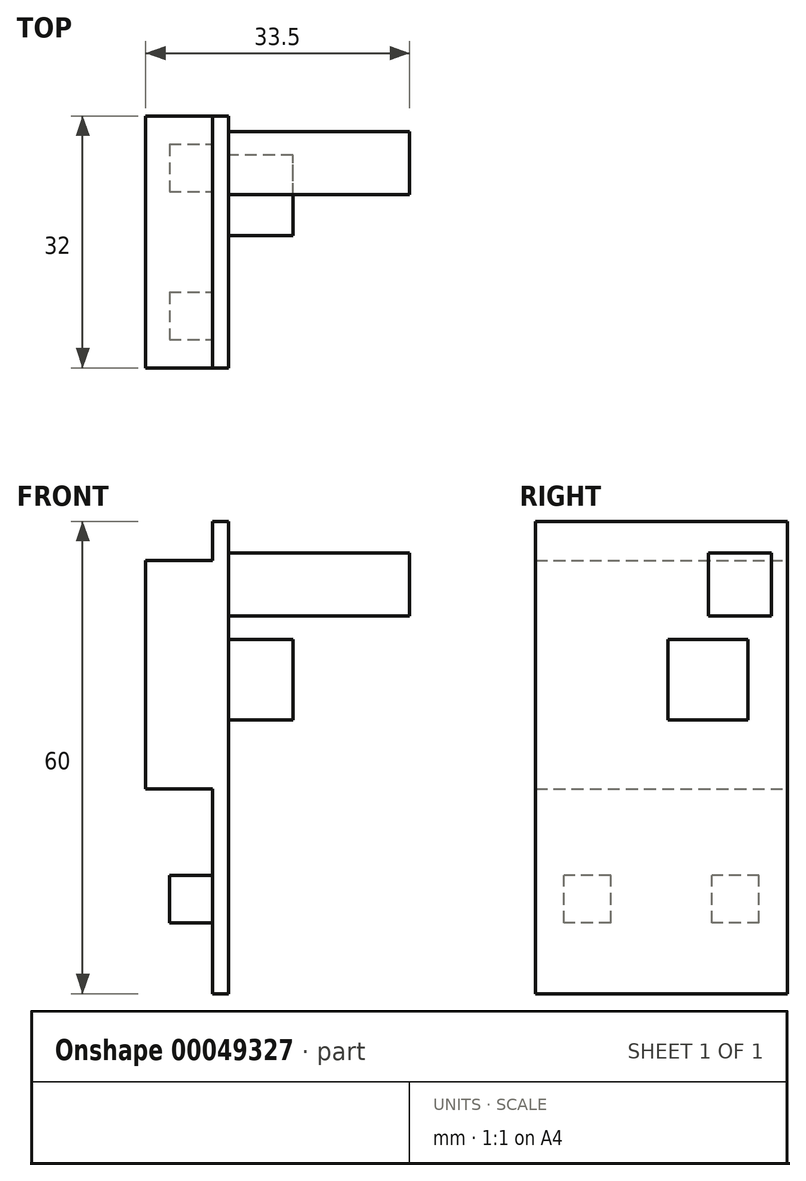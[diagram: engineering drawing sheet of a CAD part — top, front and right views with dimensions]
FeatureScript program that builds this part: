
annotation { "Feature Type Name" : "Feature", "Feature Type Description" : "" }
export const myFeature = defineFeature(function(context is Context, id is Id, definition is map)
    precondition{}
    {
        {
            var Q0;
            Q0=qCreatedBy(makeId("Right.planeOp"),FACE);
            var sketch = newSketch(context, id + "F0", { "sketchPlane" : qUnion([Q0])});
            skLineSegment(sketch, "E0.bottom", {"start": v(0, 0) * mm, "end": v(32, 0) * mm});
            skLineSegment(sketch, "E0.top", {"start": v(0, 60) * mm, "end": v(32, 60) * mm});
            skLineSegment(sketch, "E0.left", {"start": v(0, 0) * mm, "end": v(0, 60) * mm});
            skLineSegment(sketch, "E0.right", {"start": v(32, 0) * mm, "end": v(32, 60) * mm});
            skLineSegment(sketch, "E1.bottom", {"start": v(16.8, 34.8) * mm, "end": v(27, 34.8) * mm});
            skLineSegment(sketch, "E1.top", {"start": v(16.8, 45) * mm, "end": v(27, 45) * mm});
            skLineSegment(sketch, "E1.left", {"start": v(16.8, 34.8) * mm, "end": v(16.8, 45) * mm});
            skLineSegment(sketch, "E1.right", {"start": v(27, 34.8) * mm, "end": v(27, 45) * mm});
            skLineSegment(sketch, "E2.bottom", {"start": v(22, 56) * mm, "end": v(30, 56) * mm});
            skLineSegment(sketch, "E2.top", {"start": v(22, 48) * mm, "end": v(30, 48) * mm});
            skLineSegment(sketch, "E2.left", {"start": v(22, 56) * mm, "end": v(22, 48) * mm});
            skLineSegment(sketch, "E2.right", {"start": v(30, 56) * mm, "end": v(30, 48) * mm});
            skLineSegment(sketch, "E3.bottom", {"start": v(0, 26) * mm, "end": v(32, 26) * mm});
            skLineSegment(sketch, "E3.top", {"start": v(0, 55) * mm, "end": v(32, 55) * mm});
            skLineSegment(sketch, "E4.rect.bottom", {"start": v(9.6, 9) * mm, "end": v(3.6, 9) * mm});
            skLineSegment(sketch, "E4.rect.top", {"start": v(9.6, 15) * mm, "end": v(3.6, 15) * mm});
            skLineSegment(sketch, "E4.rect.left", {"start": v(9.6, 9) * mm, "end": v(9.6, 15) * mm});
            skLineSegment(sketch, "E4.rect.right", {"start": v(3.6, 9) * mm, "end": v(3.6, 15) * mm});
            skPoint(sketch, "E4.rect.middle", {"position": v(6.6, 12) * mm});
            skLineSegment(sketch, "E5.rect.bottom", {"start": v(28.4, 9) * mm, "end": v(22.4, 9) * mm});
            skLineSegment(sketch, "E5.rect.top", {"start": v(28.4, 15) * mm, "end": v(22.4, 15) * mm});
            skLineSegment(sketch, "E5.rect.left", {"start": v(28.4, 9) * mm, "end": v(28.4, 15) * mm});
            skLineSegment(sketch, "E5.rect.right", {"start": v(22.4, 9) * mm, "end": v(22.4, 15) * mm});
            skPoint(sketch, "E5.rect.middle", {"position": v(25.4, 12) * mm});
            skLineSegment(sketch, "E6", {"start": v(16, 0) * mm, "end": v(16, 60) * mm, "construction": true});
            skSolve(sketch);
        }
        {
            var Q0;
            Q0=makeQuery(id+"F0.imprint","IMPRINT",FACE,{"disambiguationData":[TD([[makeQuery(id+"F0.imprint","IMPRINT",EDGE,{"derivedFrom":sQuery(id+"F0.wireOp",EDGE,"E1.bottom")}),-1.0]])]});
            var Q1;
            Q1=makeQuery(id+"F0.imprint","IMPRINT",FACE,{"disambiguationData":[TD([[makeQuery(id+"F0.imprint","IMPRINT",EDGE,{"derivedFrom":sQuery(id+"F0.wireOp",EDGE,"E5.rect.bottom")}),-1.0]])]});
            var Q2;
            {var subQ3=sQuery(id+"F0.wireOp",EDGE,"E2.top");Q2=makeQuery(id+"F0.imprint","IMPRINT",FACE,{"disambiguationData":[TD([[makeQuery(id+"F0.imprint","IMPRINT",EDGE,{"derivedFrom":subQ3}),1.0]])]});}
            var Q3;
            {var subQ10=sQuery(id+"F0.wireOp",EDGE,"E0.top");Q3=makeQuery(id+"F0.imprint","IMPRINT",FACE,{"disambiguationData":[TD([[makeQuery(id+"F0.imprint","IMPRINT",EDGE,{"derivedFrom":subQ10}),-1.0]])]});}
            var Q4;
            {var subQ5=sQuery(id+"F0.wireOp",EDGE,"E2.bottom");Q4=makeQuery(id+"F0.imprint","IMPRINT",FACE,{"disambiguationData":[TD([[makeQuery(id+"F0.imprint","IMPRINT",EDGE,{"derivedFrom":subQ5}),-1.0]])]});}
            var Q5;
            Q5=makeQuery(id+"F0.imprint","IMPRINT",FACE,{"disambiguationData":[TD([[makeQuery(id+"F0.imprint","IMPRINT",EDGE,{"derivedFrom":sQuery(id+"F0.wireOp",EDGE,"E4.rect.bottom")}),-1.0]])]});
            var Q6;
            Q6=makeQuery(id+"F0.imprint","IMPRINT",FACE,{"disambiguationData":[TD([[makeQuery(id+"F0.imprint","IMPRINT",EDGE,{"derivedFrom":sQuery(id+"F0.wireOp",EDGE,"E1.bottom")}),1.0]])]});
            var Q7;
            {var subQ2=sQuery(id+"F0.wireOp",EDGE,"E0.bottom");Q7=makeQuery(id+"F0.imprint","IMPRINT",FACE,{"disambiguationData":[TD([[makeQuery(id+"F0.imprint","IMPRINT",EDGE,{"derivedFrom":subQ2}),1.0]])]});}
            extrude(context, id + "F1", {"entities" : qUnion([Q0, Q1, Q2, Q3, Q4, Q5, Q6, Q7]), "depth" : 2 * mm});
        }
        {
            var Q0;
            Q0=makeQuery(id+"F0.imprint","IMPRINT",FACE,{"disambiguationData":[TD([[makeQuery(id+"F0.imprint","IMPRINT",EDGE,{"derivedFrom":sQuery(id+"F0.wireOp",EDGE,"E1.bottom")}),-1.0]])]});
            var Q1;
            {var subQ3=sQuery(id+"F0.wireOp",EDGE,"E2.top");Q1=makeQuery(id+"F0.imprint","IMPRINT",FACE,{"disambiguationData":[TD([[makeQuery(id+"F0.imprint","IMPRINT",EDGE,{"derivedFrom":subQ3}),1.0]])]});}
            var Q2;
            Q2=makeQuery(id+"F0.imprint","IMPRINT",FACE,{"disambiguationData":[TD([[makeQuery(id+"F0.imprint","IMPRINT",EDGE,{"derivedFrom":sQuery(id+"F0.wireOp",EDGE,"E1.bottom")}),1.0]])]});
            extrude(context, id + "F2", {"entities" : qUnion([Q0, Q1, Q2]), "operationType" : NewBodyOperationType.ADD, "oppositeDirection" : true, "depth" : 8.5 * mm});
        }
        {
            var Q0;
            Q0=makeQuery(id+"F0.imprint","IMPRINT",FACE,{"disambiguationData":[TD([[makeQuery(id+"F0.imprint","IMPRINT",EDGE,{"derivedFrom":sQuery(id+"F0.wireOp",EDGE,"E1.bottom")}),1.0]])]});
            extrude(context, id + "F3", {"entities" : qUnion([Q0]), "depth" : 10.2 * mm});
        }
        {
            var Q0;
            {var subQ3=sQuery(id+"F0.wireOp",EDGE,"E2.top");Q0=makeQuery(id+"F0.imprint","IMPRINT",FACE,{"disambiguationData":[TD([[makeQuery(id+"F0.imprint","IMPRINT",EDGE,{"derivedFrom":subQ3}),1.0]])]});}
            var Q1;
            {var subQ5=sQuery(id+"F0.wireOp",EDGE,"E2.bottom");Q1=makeQuery(id+"F0.imprint","IMPRINT",FACE,{"disambiguationData":[TD([[makeQuery(id+"F0.imprint","IMPRINT",EDGE,{"derivedFrom":subQ5}),-1.0]])]});}
            extrude(context, id + "F4", {"entities" : qUnion([Q0, Q1]), "operationType" : NewBodyOperationType.ADD, "depth" : 25 * mm});
        }
        {
            var Q0;
            Q0=makeQuery(id+"F3.opExtrude","SWEPT_BODY",BODY,{"disambiguationData":[OSD([sQuery(id+"F0.wireOp",EDGE,"E1.bottom"),sQuery(id+"F0.wireOp",EDGE,"E1.top"),sQuery(id+"F0.wireOp",EDGE,"E1.left"),sQuery(id+"F0.wireOp",EDGE,"E1.right")])]});
            var Q1;
            Q1=makeQuery(id+"F1.opExtrude","SWEPT_BODY",BODY,{"disambiguationData":[OSD([sQuery(id+"F0.wireOp",EDGE,"E0.bottom"),sQuery(id+"F0.wireOp",EDGE,"E0.top"),sQuery(id+"F0.wireOp",EDGE,"E0.left"),sQuery(id+"F0.wireOp",EDGE,"E0.right")])]});
            booleanBodies(context, id + "F5", {"operationType" : BooleanOperationType.UNION, "tools" : qUnion([Q0, Q1])});
        }
        {
            var Q0;
            Q0=makeQuery(id+"F0.imprint","IMPRINT",FACE,{"disambiguationData":[TD([[makeQuery(id+"F0.imprint","IMPRINT",EDGE,{"derivedFrom":sQuery(id+"F0.wireOp",EDGE,"E4.rect.bottom")}),-1.0]])]});
            var Q1;
            Q1=makeQuery(id+"F0.imprint","IMPRINT",FACE,{"disambiguationData":[TD([[makeQuery(id+"F0.imprint","IMPRINT",EDGE,{"derivedFrom":sQuery(id+"F0.wireOp",EDGE,"E5.rect.bottom")}),-1.0]])]});
            extrude(context, id + "F6", {"entities" : qUnion([Q0, Q1]), "operationType" : NewBodyOperationType.ADD, "oppositeDirection" : true, "depth" : 5.5 * mm});
        }
    });
